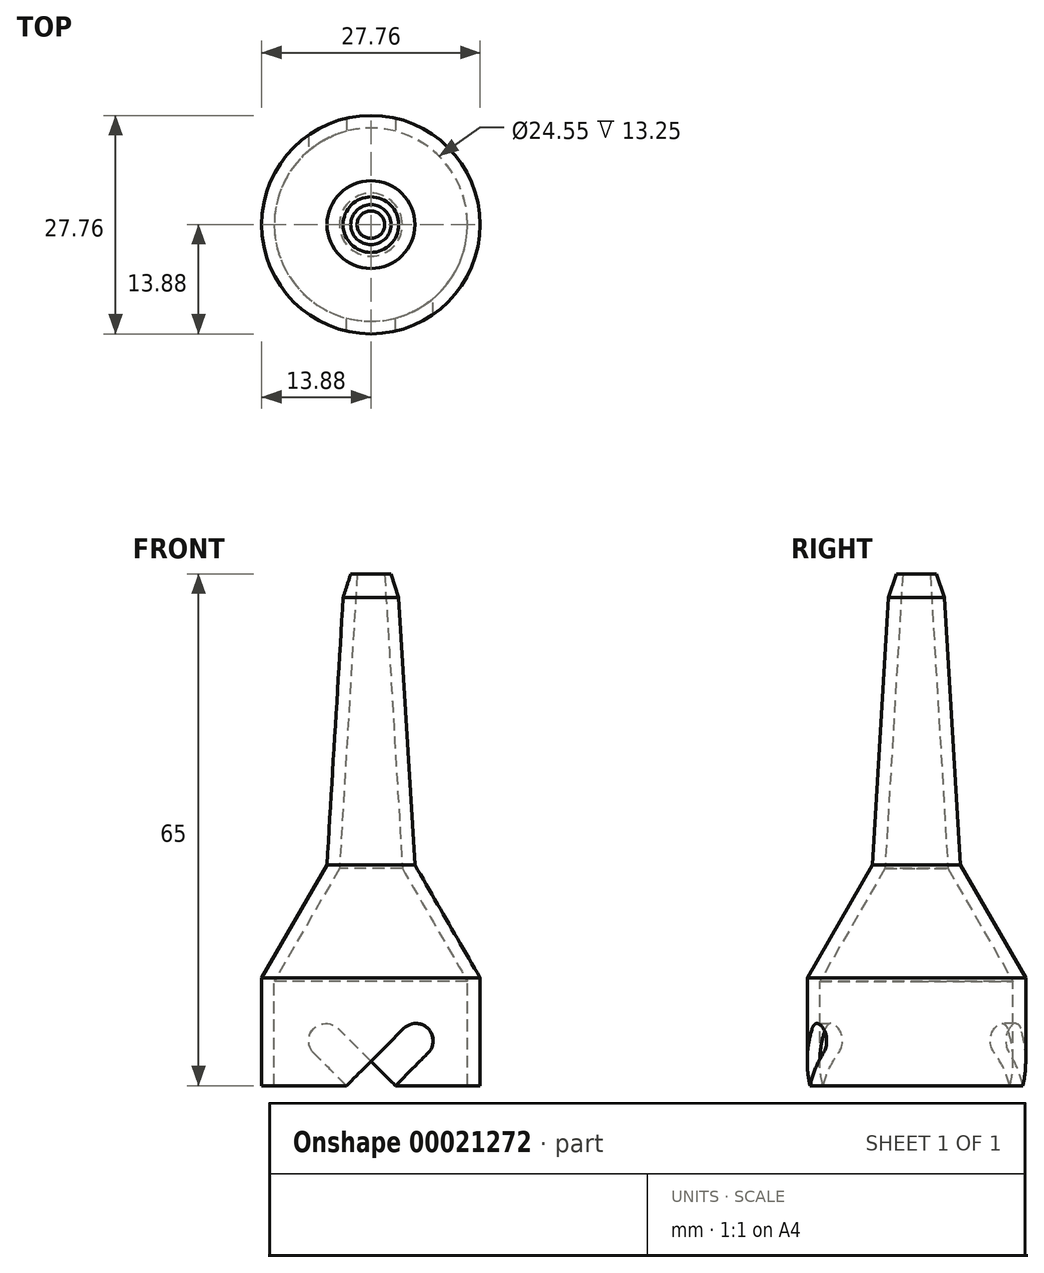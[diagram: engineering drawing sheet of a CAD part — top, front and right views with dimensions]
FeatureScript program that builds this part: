
annotation { "Feature Type Name" : "Feature", "Feature Type Description" : "" }
export const myFeature = defineFeature(function(context is Context, id is Id, definition is map)
    precondition{}
    {
        {
            var Q0;
            Q0=qCreatedBy(makeId("Front.planeOp"),FACE);
            var sketch = newSketch(context, id + "F0", { "sketchPlane" : qUnion([Q0])});
            skLineSegment(sketch, "E0", {"start": v(12.28, 0) * mm, "end": v(12.28, 13.25) * mm});
            skLineSegment(sketch, "E1", {"start": v(12.28, 13.25) * mm, "end": v(4, 27.58) * mm});
            skLineSegment(sketch, "E2", {"start": v(4, 27.58) * mm, "end": v(1.75, 65) * mm});
            skLineSegment(sketch, "E3.0", {"start": v(5.57, 28.06) * mm, "end": v(3.35, 65) * mm});
            skLineSegment(sketch, "E3.1", {"start": v(13.88, 13.68) * mm, "end": v(5.57, 28.06) * mm});
            skLineSegment(sketch, "E3.2", {"start": v(13.88, 0) * mm, "end": v(13.88, 13.68) * mm});
            skLineSegment(sketch, "E4", {"start": v(1.75, 65) * mm, "end": v(3.35, 65) * mm});
            skLineSegment(sketch, "E5", {"start": v(12.28, 0) * mm, "end": v(13.88, 0) * mm});
            skLineSegment(sketch, "E6", {"start": v(0, 65) * mm, "end": v(0, 0) * mm, "construction": true});
            skSolve(sketch);
        }
        {
            var Q0;
            Q0=makeQuery(id+"F0.imprint","IMPRINT",FACE,{"disambiguationData":[TD([[makeQuery(id+"F0.imprint","IMPRINT",EDGE,{"derivedFrom":sQuery(id+"F0.wireOp",EDGE,"E0")}),-1.0]])]});
            var Q1;
            Q1=sQuery(id+"F0.wireOp",EDGE,"E6");
            revolve(context, id + "F1", {"entities" : qUnion([Q0]), "axis" : qUnion([Q1]), "revolveType" : RevolveType.FULL});
        }
        {
            var Q0;
            Q0=qCreatedBy(makeId("Front.planeOp"),FACE);
            var sketch = newSketch(context, id + "F2", { "sketchPlane" : qUnion([Q0])});
            skLineSegment(sketch, "E7", {"start": v(-3.11, 0) * mm, "end": v(4.14, 7.26) * mm});
            skLineSegment(sketch, "E8", {"start": v(3.11, 0) * mm, "end": v(7.26, 4.14) * mm});
            skLineSegment(sketch, "E9", {"start": v(-3.11, 0) * mm, "end": v(3.11, 0) * mm});
            skArc(sketch, "E10", {"start": v(7.26, 4.14) * mm, "mid": v(7.26, 7.26) * mm, "end": v(4.14, 7.26) * mm});
            skSolve(sketch);
        }
        {
            var Q0;
            Q0 = qSketchRegion(id + "F2", true);
            extrude(context, id + "F3", {"entities" : qUnion([Q0]), "operationType" : NewBodyOperationType.REMOVE, "depth" : 15 * mm});
        }
        {
            var Q0;
            Q0=makeQuery(id+"F3.boolean.opBoolean","COPY",FACE,{"derivedFrom":makeQuery(id+"F3.opExtrude","SWEPT_FACE",FACE,{"disambiguationData":[OSD([sQuery(id+"F2.wireOp",EDGE,"E7")])]})});
            var Q1;
            Q1=makeQuery(id+"F3.boolean.opBoolean","COPY",FACE,{"derivedFrom":makeQuery(id+"F3.opExtrude","SWEPT_FACE",FACE,{"disambiguationData":[OSD([sQuery(id+"F2.wireOp",EDGE,"E10")])]})});
            var Q2;
            Q2=makeQuery(id+"F3.boolean.opBoolean","COPY",FACE,{"derivedFrom":makeQuery(id+"F3.opExtrude","SWEPT_FACE",FACE,{"disambiguationData":[OSD([sQuery(id+"F2.wireOp",EDGE,"E8")])]})});
            var Q3;
            Q3=makeQuery(id+"F1.opRevolve","SWEPT_FACE",FACE,{"disambiguationData":[OSD([sQuery(id+"F0.wireOp",EDGE,"E0")])]});
            circularPattern(context, id + "F4", {"faces" : qUnion([Q0, Q1, Q2]), "axis" : qUnion([Q3]), "angle" : 180 * degree, "instanceCount" : 2, "patternType" : PatternType.FACE});
        }
        {
            var Q0;
            Q0=makeQuery(id+"F1.opRevolve","SWEPT_EDGE",EDGE,{"disambiguationData":[OSD([sQuery(id+"F0.wireOp",EDGE,"E3.0"),sQuery(id+"F0.wireOp",EDGE,"E4")])]});
            chamfer(context, id + "F5", {"entities" : qUnion([Q0]), "chamferType" : ChamferType.TWO_OFFSETS, "width1" : .8 * mm, "oppositeDirection" : false, "width2" : 3 * mm, "tangentPropagation" : true});
        }
    });
